FCSTD DOCUMENT  (FreeCAD 0.18.1R)
Label: Clock_idea_outline
License: All rights reserved
LicenseURL: http://en.wikipedia.org/wiki/All_rights_reserved
objects: Sketcher::SketchObject×1, PartDesign::Body×1
note: 2 computed .brp shape members not serialized (recipe doc carries the construction recipe); baked Part::Feature solids carry a one-line shape summary decoded from their .brp

FEATURE [Sketcher::SketchObject] Sketch
  MapMode = 5
  Support = -> [XY_Plane]
  sketch-geometry (292):
    g0: LineSegment StartX=0 StartY=0 StartZ=0 EndX=100 EndY=0 EndZ=0
    g1: LineSegment StartX=100 StartY=0 StartZ=0 EndX=100 EndY=50 EndZ=0
    g2: LineSegment StartX=100 StartY=50 StartZ=0 EndX=0 EndY=50 EndZ=0
    g3: LineSegment StartX=0 StartY=50 StartZ=0 EndX=0 EndY=0 EndZ=0
    g4: LineSegment StartX=1.68333 StartY=3 StartZ=0 EndX=4.98333 EndY=3 EndZ=0
    g5: LineSegment StartX=4.98333 StartY=3 StartZ=0 EndX=4.98333 EndY=5.1 EndZ=0
    g6: LineSegment StartX=4.98333 StartY=5.1 StartZ=0 EndX=1.68333 EndY=5.1 EndZ=0
    g7: LineSegment StartX=1.68333 StartY=5.1 StartZ=0 EndX=1.68333 EndY=3 EndZ=0
    g8: LineSegment StartX=8.35 StartY=3 StartZ=0 EndX=11.65 EndY=3 EndZ=0
    g9: LineSegment StartX=11.65 StartY=3 StartZ=0 EndX=11.65 EndY=5.1 EndZ=0
    g10: LineSegment StartX=11.65 StartY=5.1 StartZ=0 EndX=8.35 EndY=5.1 EndZ=0
    g11: LineSegment StartX=8.35 StartY=5.1 StartZ=0 EndX=8.35 EndY=3 EndZ=0
    g12: LineSegment StartX=15.0167 StartY=3 StartZ=0 EndX=18.3167 EndY=3 EndZ=0
    g13: LineSegment StartX=18.3167 StartY=3 StartZ=0 EndX=18.3167 EndY=5.1 EndZ=0
    g14: LineSegment StartX=18.3167 StartY=5.1 StartZ=0 EndX=15.0167 EndY=5.1 EndZ=0
    g15: LineSegment StartX=15.0167 StartY=5.1 StartZ=0 EndX=15.0167 EndY=3 EndZ=0
    g16: LineSegment StartX=21.6833 StartY=3 StartZ=0 EndX=24.9833 EndY=3 EndZ=0
    g17: LineSegment StartX=24.9833 StartY=3 StartZ=0 EndX=24.9833 EndY=5.1 EndZ=0
    g18: LineSegment StartX=24.9833 StartY=5.1 StartZ=0 EndX=21.6833 EndY=5.1 EndZ=0
    g19: LineSegment StartX=21.6833 StartY=5.1 StartZ=0 EndX=21.6833 EndY=3 EndZ=0
    g20: LineSegment StartX=28.35 StartY=3 StartZ=0 EndX=31.65 EndY=3 EndZ=0
    g21: LineSegment StartX=31.65 StartY=3 StartZ=0 EndX=31.65 EndY=5.1 EndZ=0
    g22: LineSegment StartX=31.65 StartY=5.1 StartZ=0 EndX=28.35 EndY=5.1 EndZ=0
    g23: LineSegment StartX=28.35 StartY=5.1 StartZ=0 EndX=28.35 EndY=3 EndZ=0
    g24: LineSegment StartX=35.0167 StartY=3 StartZ=0 EndX=38.3167 EndY=3 EndZ=0
    g25: LineSegment StartX=38.3167 StartY=3 StartZ=0 EndX=38.3167 EndY=5.1 EndZ=0
    g26: LineSegment StartX=38.3167 StartY=5.1 StartZ=0 EndX=35.0167 EndY=5.1 EndZ=0
    g27: LineSegment StartX=35.0167 StartY=5.1 StartZ=0 EndX=35.0167 EndY=3 EndZ=0
    g28: LineSegment StartX=41.6833 StartY=3 StartZ=0 EndX=44.9833 EndY=3 EndZ=0
    g29: LineSegment StartX=44.9833 StartY=3 StartZ=0 EndX=44.9833 EndY=5.1 EndZ=0
    g30: LineSegment StartX=44.9833 StartY=5.1 StartZ=0 EndX=41.6833 EndY=5.1 EndZ=0
    g31: LineSegment StartX=41.6833 StartY=5.1 StartZ=0 EndX=41.6833 EndY=3 EndZ=0
    g32: LineSegment StartX=48.35 StartY=3 StartZ=0 EndX=51.65 EndY=3 EndZ=0
    g33: LineSegment StartX=51.65 StartY=3 StartZ=0 EndX=51.65 EndY=5.1 EndZ=0
    g34: LineSegment StartX=51.65 StartY=5.1 StartZ=0 EndX=48.35 EndY=5.1 EndZ=0
    g35: LineSegment StartX=48.35 StartY=5.1 StartZ=0 EndX=48.35 EndY=3 EndZ=0
    g36: LineSegment StartX=55.0167 StartY=3 StartZ=0 EndX=58.3167 EndY=3 EndZ=0
    g37: LineSegment StartX=58.3167 StartY=3 StartZ=0 EndX=58.3167 EndY=5.1 EndZ=0
    g38: LineSegment StartX=58.3167 StartY=5.1 StartZ=0 EndX=55.0167 EndY=5.1 EndZ=0
    g39: LineSegment StartX=55.0167 StartY=5.1 StartZ=0 EndX=55.0167 EndY=3 EndZ=0
    g40: LineSegment StartX=61.6833 StartY=3 StartZ=0 EndX=64.9833 EndY=3 EndZ=0
    g41: LineSegment StartX=64.9833 StartY=3 StartZ=0 EndX=64.9833 EndY=5.1 EndZ=0
    g42: LineSegment StartX=64.9833 StartY=5.1 StartZ=0 EndX=61.6833 EndY=5.1 EndZ=0
    g43: LineSegment StartX=61.6833 StartY=5.1 StartZ=0 EndX=61.6833 EndY=3 EndZ=0
    g44: LineSegment StartX=68.35 StartY=3 StartZ=0 EndX=71.65 EndY=3 EndZ=0
    g45: LineSegment StartX=71.65 StartY=3 StartZ=0 EndX=71.65 EndY=5.1 EndZ=0
    g46: LineSegment StartX=71.65 StartY=5.1 StartZ=0 EndX=68.35 EndY=5.1 EndZ=0
    g47: LineSegment StartX=68.35 StartY=5.1 StartZ=0 EndX=68.35 EndY=3 EndZ=0
    g48: LineSegment StartX=75.0167 StartY=3 StartZ=0 EndX=78.3167 EndY=3 EndZ=0
    g49: LineSegment StartX=78.3167 StartY=3 StartZ=0 EndX=78.3167 EndY=5.1 EndZ=0
    g50: LineSegment StartX=78.3167 StartY=5.1 StartZ=0 EndX=75.0167 EndY=5.1 EndZ=0
    g51: LineSegment StartX=75.0167 StartY=5.1 StartZ=0 EndX=75.0167 EndY=3 EndZ=0
    g52: LineSegment StartX=81.6833 StartY=3 StartZ=0 EndX=84.9833 EndY=3 EndZ=0
    g53: LineSegment StartX=84.9833 StartY=3 StartZ=0 EndX=84.9833 EndY=5.1 EndZ=0
    g54: LineSegment StartX=84.9833 StartY=5.1 StartZ=0 EndX=81.6833 EndY=5.1 EndZ=0
    g55: LineSegment StartX=81.6833 StartY=5.1 StartZ=0 EndX=81.6833 EndY=3 EndZ=0
    g56: LineSegment StartX=88.35 StartY=3 StartZ=0 EndX=91.65 EndY=3 EndZ=0
    g57: LineSegment StartX=91.65 StartY=3 StartZ=0 EndX=91.65 EndY=5.1 EndZ=0
    g58: LineSegment StartX=91.65 StartY=5.1 StartZ=0 EndX=88.35 EndY=5.1 EndZ=0
    g59: LineSegment StartX=88.35 StartY=5.1 StartZ=0 EndX=88.35 EndY=3 EndZ=0
    g60: LineSegment StartX=95.0167 StartY=3 StartZ=0 EndX=98.3167 EndY=3 EndZ=0
    g61: LineSegment StartX=98.3167 StartY=3 StartZ=0 EndX=98.3167 EndY=5.1 EndZ=0
    g62: LineSegment StartX=98.3167 StartY=5.1 StartZ=0 EndX=95.0167 EndY=5.1 EndZ=0
    g63: LineSegment StartX=95.0167 StartY=5.1 StartZ=0 EndX=95.0167 EndY=3 EndZ=0
    g64: LineSegment StartX=1.68333 StartY=8.1 StartZ=0 EndX=4.98333 EndY=8.1 EndZ=0
    g65: LineSegment StartX=4.98333 StartY=8.1 StartZ=0 EndX=4.98333 EndY=10.2 EndZ=0
    g66: LineSegment StartX=4.98333 StartY=10.2 StartZ=0 EndX=1.68333 EndY=10.2 EndZ=0
    g67: LineSegment StartX=1.68333 StartY=10.2 StartZ=0 EndX=1.68333 EndY=8.1 EndZ=0
    g68: LineSegment StartX=8.35 StartY=8.1 StartZ=0 EndX=11.65 EndY=8.1 EndZ=0
    g69: LineSegment StartX=11.65 StartY=8.1 StartZ=0 EndX=11.65 EndY=10.2 EndZ=0
    g70: LineSegment StartX=11.65 StartY=10.2 StartZ=0 EndX=8.35 EndY=10.2 EndZ=0
    g71: LineSegment StartX=8.35 StartY=10.2 StartZ=0 EndX=8.35 EndY=8.1 EndZ=0
    g72: LineSegment StartX=15.0167 StartY=8.1 StartZ=0 EndX=18.3167 EndY=8.1 EndZ=0
    g73: LineSegment StartX=18.3167 StartY=8.1 StartZ=0 EndX=18.3167 EndY=10.2 EndZ=0
    g74: LineSegment StartX=18.3167 StartY=10.2 StartZ=0 EndX=15.0167 EndY=10.2 EndZ=0
    g75: LineSegment StartX=15.0167 StartY=10.2 StartZ=0 EndX=15.0167 EndY=8.1 EndZ=0
    g76: LineSegment StartX=21.6833 StartY=8.1 StartZ=0 EndX=24.9833 EndY=8.1 EndZ=0
    g77: LineSegment StartX=24.9833 StartY=8.1 StartZ=0 EndX=24.9833 EndY=10.2 EndZ=0
    g78: LineSegment StartX=24.9833 StartY=10.2 StartZ=0 EndX=21.6833 EndY=10.2 EndZ=0
    g79: LineSegment StartX=21.6833 StartY=10.2 StartZ=0 EndX=21.6833 EndY=8.1 EndZ=0
    g80: LineSegment StartX=28.35 StartY=8.1 StartZ=0 EndX=31.65 EndY=8.1 EndZ=0
    g81: LineSegment StartX=31.65 StartY=8.1 StartZ=0 EndX=31.65 EndY=10.2 EndZ=0
    g82: LineSegment StartX=31.65 StartY=10.2 StartZ=0 EndX=28.35 EndY=10.2 EndZ=0
    g83: LineSegment StartX=28.35 StartY=10.2 StartZ=0 EndX=28.35 EndY=8.1 EndZ=0
    g84: LineSegment StartX=35.0167 StartY=8.1 StartZ=0 EndX=38.3167 EndY=8.1 EndZ=0
    g85: LineSegment StartX=38.3167 StartY=8.1 StartZ=0 EndX=38.3167 EndY=10.2 EndZ=0
    g86: LineSegment StartX=38.3167 StartY=10.2 StartZ=0 EndX=35.0167 EndY=10.2 EndZ=0
    g87: LineSegment StartX=35.0167 StartY=10.2 StartZ=0 EndX=35.0167 EndY=8.1 EndZ=0
    g88: LineSegment StartX=41.6833 StartY=8.1 StartZ=0 EndX=44.9833 EndY=8.1 EndZ=0
    g89: LineSegment StartX=44.9833 StartY=8.1 StartZ=0 EndX=44.9833 EndY=10.2 EndZ=0
    g90: LineSegment StartX=44.9833 StartY=10.2 StartZ=0 EndX=41.6833 EndY=10.2 EndZ=0
    g91: LineSegment StartX=41.6833 StartY=10.2 StartZ=0 EndX=41.6833 EndY=8.1 EndZ=0
    g92: LineSegment StartX=48.35 StartY=8.1 StartZ=0 EndX=51.65 EndY=8.1 EndZ=0
    g93: LineSegment StartX=51.65 StartY=8.1 StartZ=0 EndX=51.65 EndY=10.2 EndZ=0
    g94: LineSegment StartX=51.65 StartY=10.2 StartZ=0 EndX=48.35 EndY=10.2 EndZ=0
    g95: LineSegment StartX=48.35 StartY=10.2 StartZ=0 EndX=48.35 EndY=8.1 EndZ=0
    g96: LineSegment StartX=55.0167 StartY=8.1 StartZ=0 EndX=58.3167 EndY=8.1 EndZ=0
    g97: LineSegment StartX=58.3167 StartY=8.1 StartZ=0 EndX=58.3167 EndY=10.2 EndZ=0
    g98: LineSegment StartX=58.3167 StartY=10.2 StartZ=0 EndX=55.0167 EndY=10.2 EndZ=0
    g99: LineSegment StartX=55.0167 StartY=10.2 StartZ=0 EndX=55.0167 EndY=8.1 EndZ=0
    g100: LineSegment StartX=61.6833 StartY=8.1 StartZ=0 EndX=64.9833 EndY=8.1 EndZ=0
    g101: LineSegment StartX=64.9833 StartY=8.1 StartZ=0 EndX=64.9833 EndY=10.2 EndZ=0
    g102: LineSegment StartX=64.9833 StartY=10.2 StartZ=0 EndX=61.6833 EndY=10.2 EndZ=0
    g103: LineSegment StartX=61.6833 StartY=10.2 StartZ=0 EndX=61.6833 EndY=8.1 EndZ=0
    g104: LineSegment StartX=68.35 StartY=8.1 StartZ=0 EndX=71.65 EndY=8.1 EndZ=0
    g105: LineSegment StartX=71.65 StartY=8.1 StartZ=0 EndX=71.65 EndY=10.2 EndZ=0
    g106: LineSegment StartX=71.65 StartY=10.2 StartZ=0 EndX=68.35 EndY=10.2 EndZ=0
    g107: LineSegment StartX=68.35 StartY=10.2 StartZ=0 EndX=68.35 EndY=8.1 EndZ=0
    g108: LineSegment StartX=75.0167 StartY=8.1 StartZ=0 EndX=78.3167 EndY=8.1 EndZ=0
    g109: LineSegment StartX=78.3167 StartY=8.1 StartZ=0 EndX=78.3167 EndY=10.2 EndZ=0
    g110: LineSegment StartX=78.3167 StartY=10.2 StartZ=0 EndX=75.0167 EndY=10.2 EndZ=0
    g111: LineSegment StartX=75.0167 StartY=10.2 StartZ=0 EndX=75.0167 EndY=8.1 EndZ=0
    g112: LineSegment StartX=81.6833 StartY=8.1 StartZ=0 EndX=84.9833 EndY=8.1 EndZ=0
    g113: LineSegment StartX=84.9833 StartY=8.1 StartZ=0 EndX=84.9833 EndY=10.2 EndZ=0
    g114: LineSegment StartX=84.9833 StartY=10.2 StartZ=0 EndX=81.6833 EndY=10.2 EndZ=0
    g115: LineSegment StartX=81.6833 StartY=10.2 StartZ=0 EndX=81.6833 EndY=8.1 EndZ=0
    g116: LineSegment StartX=88.35 StartY=8.1 StartZ=0 EndX=91.65 EndY=8.1 EndZ=0
    g117: LineSegment StartX=91.65 StartY=8.1 StartZ=0 EndX=91.65 EndY=10.2 EndZ=0
    g118: LineSegment StartX=91.65 StartY=10.2 StartZ=0 EndX=88.35 EndY=10.2 EndZ=0
    g119: LineSegment StartX=88.35 StartY=10.2 StartZ=0 EndX=88.35 EndY=8.1 EndZ=0
    g120: LineSegment StartX=95.0167 StartY=8.1 StartZ=0 EndX=98.3167 EndY=8.1 EndZ=0
    g121: LineSegment StartX=98.3167 StartY=8.1 StartZ=0 EndX=98.3167 EndY=10.2 EndZ=0
    g122: LineSegment StartX=98.3167 StartY=10.2 StartZ=0 EndX=95.0167 EndY=10.2 EndZ=0
    g123: LineSegment StartX=95.0167 StartY=10.2 StartZ=0 EndX=95.0167 EndY=8.1 EndZ=0
    g124: LineSegment StartX=1.68333 StartY=13.2 StartZ=0 EndX=4.98333 EndY=13.2 EndZ=0
    g125: LineSegment StartX=4.98333 StartY=13.2 StartZ=0 EndX=4.98333 EndY=15.3 EndZ=0
    g126: LineSegment StartX=4.98333 StartY=15.3 StartZ=0 EndX=1.68333 EndY=15.3 EndZ=0
    g127: LineSegment StartX=1.68333 StartY=15.3 StartZ=0 EndX=1.68333 EndY=13.2 EndZ=0
    g128: LineSegment StartX=8.35 StartY=13.2 StartZ=0 EndX=11.65 EndY=13.2 EndZ=0
    g129: LineSegment StartX=11.65 StartY=13.2 StartZ=0 EndX=11.65 EndY=15.3 EndZ=0
    g130: LineSegment StartX=11.65 StartY=15.3 StartZ=0 EndX=8.35 EndY=15.3 EndZ=0
    g131: LineSegment StartX=8.35 StartY=15.3 StartZ=0 EndX=8.35 EndY=13.2 EndZ=0
    g132: LineSegment StartX=15.0167 StartY=13.2 StartZ=0 EndX=18.3167 EndY=13.2 EndZ=0
    g133: LineSegment StartX=18.3167 StartY=13.2 StartZ=0 EndX=18.3167 EndY=15.3 EndZ=0
    g134: LineSegment StartX=18.3167 StartY=15.3 StartZ=0 EndX=15.0167 EndY=15.3 EndZ=0
    g135: LineSegment StartX=15.0167 StartY=15.3 StartZ=0 EndX=15.0167 EndY=13.2 EndZ=0
    g136: LineSegment StartX=21.6833 StartY=13.2 StartZ=0 EndX=24.9833 EndY=13.2 EndZ=0
    g137: LineSegment StartX=24.9833 StartY=13.2 StartZ=0 EndX=24.9833 EndY=15.3 EndZ=0
    g138: LineSegment StartX=24.9833 StartY=15.3 StartZ=0 EndX=21.6833 EndY=15.3 EndZ=0
    g139: LineSegment StartX=21.6833 StartY=15.3 StartZ=0 EndX=21.6833 EndY=13.2 EndZ=0
    g140: LineSegment StartX=28.35 StartY=13.2 StartZ=0 EndX=31.65 EndY=13.2 EndZ=0
    g141: LineSegment StartX=31.65 StartY=13.2 StartZ=0 EndX=31.65 EndY=15.3 EndZ=0
    g142: LineSegment StartX=31.65 StartY=15.3 StartZ=0 EndX=28.35 EndY=15.3 EndZ=0
    g143: LineSegment StartX=28.35 StartY=15.3 StartZ=0 EndX=28.35 EndY=13.2 EndZ=0
    g144: LineSegment StartX=35.0167 StartY=13.2 StartZ=0 EndX=38.3167 EndY=13.2 EndZ=0
    g145: LineSegment StartX=38.3167 StartY=13.2 StartZ=0 EndX=38.3167 EndY=15.3 EndZ=0
    g146: LineSegment StartX=38.3167 StartY=15.3 StartZ=0 EndX=35.0167 EndY=15.3 EndZ=0
    g147: LineSegment StartX=35.0167 StartY=15.3 StartZ=0 EndX=35.0167 EndY=13.2 EndZ=0
    g148: LineSegment StartX=41.6833 StartY=13.2 StartZ=0 EndX=44.9833 EndY=13.2 EndZ=0
    g149: LineSegment StartX=44.9833 StartY=13.2 StartZ=0 EndX=44.9833 EndY=15.3 EndZ=0
    g150: LineSegment StartX=44.9833 StartY=15.3 StartZ=0 EndX=41.6833 EndY=15.3 EndZ=0
    g151: LineSegment StartX=41.6833 StartY=15.3 StartZ=0 EndX=41.6833 EndY=13.2 EndZ=0
    g152: LineSegment StartX=48.35 StartY=13.2 StartZ=0 EndX=51.65 EndY=13.2 EndZ=0
    g153: LineSegment StartX=51.65 StartY=13.2 StartZ=0 EndX=51.65 EndY=15.3 EndZ=0
    g154: LineSegment StartX=51.65 StartY=15.3 StartZ=0 EndX=48.35 EndY=15.3 EndZ=0
    g155: LineSegment StartX=48.35 StartY=15.3 StartZ=0 EndX=48.35 EndY=13.2 EndZ=0
    g156: LineSegment StartX=55.0167 StartY=13.2 StartZ=0 EndX=58.3167 EndY=13.2 EndZ=0
    g157: LineSegment StartX=58.3167 StartY=13.2 StartZ=0 EndX=58.3167 EndY=15.3 EndZ=0
    g158: LineSegment StartX=58.3167 StartY=15.3 StartZ=0 EndX=55.0167 EndY=15.3 EndZ=0
    g159: LineSegment StartX=55.0167 StartY=15.3 StartZ=0 EndX=55.0167 EndY=13.2 EndZ=0
    g160: LineSegment StartX=61.6833 StartY=13.2 StartZ=0 EndX=64.9833 EndY=13.2 EndZ=0
    g161: LineSegment StartX=64.9833 StartY=13.2 StartZ=0 EndX=64.9833 EndY=15.3 EndZ=0
    g162: LineSegment StartX=64.9833 StartY=15.3 StartZ=0 EndX=61.6833 EndY=15.3 EndZ=0
    g163: LineSegment StartX=61.6833 StartY=15.3 StartZ=0 EndX=61.6833 EndY=13.2 EndZ=0
    g164: LineSegment StartX=68.35 StartY=13.2 StartZ=0 EndX=71.65 EndY=13.2 EndZ=0
    g165: LineSegment StartX=71.65 StartY=13.2 StartZ=0 EndX=71.65 EndY=15.3 EndZ=0
    g166: LineSegment StartX=71.65 StartY=15.3 StartZ=0 EndX=68.35 EndY=15.3 EndZ=0
    g167: LineSegment StartX=68.35 StartY=15.3 StartZ=0 EndX=68.35 EndY=13.2 EndZ=0
    g168: LineSegment StartX=75.0167 StartY=13.2 StartZ=0 EndX=78.3167 EndY=13.2 EndZ=0
    g169: LineSegment StartX=78.3167 StartY=13.2 StartZ=0 EndX=78.3167 EndY=15.3 EndZ=0
    g170: LineSegment StartX=78.3167 StartY=15.3 StartZ=0 EndX=75.0167 EndY=15.3 EndZ=0
    g171: LineSegment StartX=75.0167 StartY=15.3 StartZ=0 EndX=75.0167 EndY=13.2 EndZ=0
    g172: LineSegment StartX=81.6833 StartY=13.2 StartZ=0 EndX=84.9833 EndY=13.2 EndZ=0
    g173: LineSegment StartX=84.9833 StartY=13.2 StartZ=0 EndX=84.9833 EndY=15.3 EndZ=0
    g174: LineSegment StartX=84.9833 StartY=15.3 StartZ=0 EndX=81.6833 EndY=15.3 EndZ=0
    g175: LineSegment StartX=81.6833 StartY=15.3 StartZ=0 EndX=81.6833 EndY=13.2 EndZ=0
    g176: LineSegment StartX=88.35 StartY=13.2 StartZ=0 EndX=91.65 EndY=13.2 EndZ=0
    g177: LineSegment StartX=91.65 StartY=13.2 StartZ=0 EndX=91.65 EndY=15.3 EndZ=0
    g178: LineSegment StartX=91.65 StartY=15.3 StartZ=0 EndX=88.35 EndY=15.3 EndZ=0
    g179: LineSegment StartX=88.35 StartY=15.3 StartZ=0 EndX=88.35 EndY=13.2 EndZ=0
    g180: LineSegment StartX=95.0167 StartY=13.2 StartZ=0 EndX=98.3167 EndY=13.2 EndZ=0
    g181: LineSegment StartX=98.3167 StartY=13.2 StartZ=0 EndX=98.3167 EndY=15.3 EndZ=0
    g182: LineSegment StartX=98.3167 StartY=15.3 StartZ=0 EndX=95.0167 EndY=15.3 EndZ=0
    g183: LineSegment StartX=95.0167 StartY=15.3 StartZ=0 EndX=95.0167 EndY=13.2 EndZ=0
    g184: LineSegment StartX=2.51667 StartY=25.5 StartZ=0 EndX=5.81667 EndY=25.5 EndZ=0
    g185: LineSegment StartX=5.81667 StartY=25.5 StartZ=0 EndX=5.81667 EndY=27.6 EndZ=0
    g186: LineSegment StartX=5.81667 StartY=27.6 StartZ=0 EndX=2.51667 EndY=27.6 EndZ=0
    g187: LineSegment StartX=2.51667 StartY=27.6 StartZ=0 EndX=2.51667 EndY=25.5 EndZ=0
    g188: LineSegment StartX=10.85 StartY=25.5 StartZ=0 EndX=14.15 EndY=25.5 EndZ=0
    g189: LineSegment StartX=14.15 StartY=25.5 StartZ=0 EndX=14.15 EndY=27.6 EndZ=0
    g190: LineSegment StartX=14.15 StartY=27.6 StartZ=0 EndX=10.85 EndY=27.6 EndZ=0
    g191: LineSegment StartX=10.85 StartY=27.6 StartZ=0 EndX=10.85 EndY=25.5 EndZ=0
    g192: LineSegment StartX=19.1833 StartY=25.5 StartZ=0 EndX=22.4833 EndY=25.5 EndZ=0
    g193: LineSegment StartX=22.4833 StartY=25.5 StartZ=0 EndX=22.4833 EndY=27.6 EndZ=0
    g194: LineSegment StartX=22.4833 StartY=27.6 StartZ=0 EndX=19.1833 EndY=27.6 EndZ=0
    g195: LineSegment StartX=19.1833 StartY=27.6 StartZ=0 EndX=19.1833 EndY=25.5 EndZ=0
    g196: LineSegment StartX=27.5167 StartY=25.5 StartZ=0 EndX=30.8167 EndY=25.5 EndZ=0
    g197: LineSegment StartX=30.8167 StartY=25.5 StartZ=0 EndX=30.8167 EndY=27.6 EndZ=0
    g198: LineSegment StartX=30.8167 StartY=27.6 StartZ=0 EndX=27.5167 EndY=27.6 EndZ=0
    g199: LineSegment StartX=27.5167 StartY=27.6 StartZ=0 EndX=27.5167 EndY=25.5 EndZ=0
    g200: LineSegment StartX=35.85 StartY=25.5 StartZ=0 EndX=39.15 EndY=25.5 EndZ=0
    g201: LineSegment StartX=39.15 StartY=25.5 StartZ=0 EndX=39.15 EndY=27.6 EndZ=0
    g202: LineSegment StartX=39.15 StartY=27.6 StartZ=0 EndX=35.85 EndY=27.6 EndZ=0
    g203: LineSegment StartX=35.85 StartY=27.6 StartZ=0 EndX=35.85 EndY=25.5 EndZ=0
    g204: LineSegment StartX=44.1833 StartY=25.5 StartZ=0 EndX=47.4833 EndY=25.5 EndZ=0
    g205: LineSegment StartX=47.4833 StartY=25.5 StartZ=0 EndX=47.4833 EndY=27.6 EndZ=0
    g206: LineSegment StartX=47.4833 StartY=27.6 StartZ=0 EndX=44.1833 EndY=27.6 EndZ=0
    g207: LineSegment StartX=44.1833 StartY=27.6 StartZ=0 EndX=44.1833 EndY=25.5 EndZ=0
    g208: LineSegment StartX=52.5167 StartY=25.5 StartZ=0 EndX=55.8167 EndY=25.5 EndZ=0
    g209: LineSegment StartX=55.8167 StartY=25.5 StartZ=0 EndX=55.8167 EndY=27.6 EndZ=0
    g210: LineSegment StartX=55.8167 StartY=27.6 StartZ=0 EndX=52.5167 EndY=27.6 EndZ=0
    g211: LineSegment StartX=52.5167 StartY=27.6 StartZ=0 EndX=52.5167 EndY=25.5 EndZ=0
    g212: LineSegment StartX=60.85 StartY=25.5 StartZ=0 EndX=64.15 EndY=25.5 EndZ=0
    g213: LineSegment StartX=64.15 StartY=25.5 StartZ=0 EndX=64.15 EndY=27.6 EndZ=0
    g214: LineSegment StartX=64.15 StartY=27.6 StartZ=0 EndX=60.85 EndY=27.6 EndZ=0
    g215: LineSegment StartX=60.85 StartY=27.6 StartZ=0 EndX=60.85 EndY=25.5 EndZ=0
    g216: LineSegment StartX=69.1833 StartY=25.5 StartZ=0 EndX=72.4833 EndY=25.5 EndZ=0
    g217: LineSegment StartX=72.4833 StartY=25.5 StartZ=0 EndX=72.4833 EndY=27.6 EndZ=0
    g218: LineSegment StartX=72.4833 StartY=27.6 StartZ=0 EndX=69.1833 EndY=27.6 EndZ=0
    g219: LineSegment StartX=69.1833 StartY=27.6 StartZ=0 EndX=69.1833 EndY=25.5 EndZ=0
    g220: LineSegment StartX=77.5167 StartY=25.5 StartZ=0 EndX=80.8167 EndY=25.5 EndZ=0
    g221: LineSegment StartX=80.8167 StartY=25.5 StartZ=0 EndX=80.8167 EndY=27.6 EndZ=0
    g222: LineSegment StartX=80.8167 StartY=27.6 StartZ=0 EndX=77.5167 EndY=27.6 EndZ=0
    g223: LineSegment StartX=77.5167 StartY=27.6 StartZ=0 EndX=77.5167 EndY=25.5 EndZ=0
    g224: LineSegment StartX=85.85 StartY=25.5 StartZ=0 EndX=89.15 EndY=25.5 EndZ=0
    g225: LineSegment StartX=89.15 StartY=25.5 StartZ=0 EndX=89.15 EndY=27.6 EndZ=0
    g226: LineSegment StartX=89.15 StartY=27.6 StartZ=0 EndX=85.85 EndY=27.6 EndZ=0
    g227: LineSegment StartX=85.85 StartY=27.6 StartZ=0 EndX=85.85 EndY=25.5 EndZ=0
    g228: LineSegment StartX=94.1833 StartY=25.5 StartZ=0 EndX=97.4833 EndY=25.5 EndZ=0
    g229: LineSegment StartX=97.4833 StartY=25.5 StartZ=0 EndX=97.4833 EndY=27.6 EndZ=0
    g230: LineSegment StartX=97.4833 StartY=27.6 StartZ=0 EndX=94.1833 EndY=27.6 EndZ=0
    g231: LineSegment StartX=94.1833 StartY=27.6 StartZ=0 EndX=94.1833 EndY=25.5 EndZ=0
    g232: LineSegment StartX=1.68333 StartY=18.3 StartZ=0 EndX=4.98333 EndY=18.3 EndZ=0
    g233: LineSegment StartX=4.98333 StartY=18.3 StartZ=0 EndX=4.98333 EndY=20.4 EndZ=0
    g234: LineSegment StartX=4.98333 StartY=20.4 StartZ=0 EndX=1.68333 EndY=20.4 EndZ=0
    g235: LineSegment StartX=1.68333 StartY=20.4 StartZ=0 EndX=1.68333 EndY=18.3 EndZ=0
    g236: LineSegment StartX=8.35 StartY=18.3 StartZ=0 EndX=11.65 EndY=18.3 EndZ=0
    g237: LineSegment StartX=11.65 StartY=18.3 StartZ=0 EndX=11.65 EndY=20.4 EndZ=0
    g238: LineSegment StartX=11.65 StartY=20.4 StartZ=0 EndX=8.35 EndY=20.4 EndZ=0
    g239: LineSegment StartX=8.35 StartY=20.4 StartZ=0 EndX=8.35 EndY=18.3 EndZ=0
    g240: LineSegment StartX=15.0167 StartY=18.3 StartZ=0 EndX=18.3167 EndY=18.3 EndZ=0
    g241: LineSegment StartX=18.3167 StartY=18.3 StartZ=0 EndX=18.3167 EndY=20.4 EndZ=0
    g242: LineSegment StartX=18.3167 StartY=20.4 StartZ=0 EndX=15.0167 EndY=20.4 EndZ=0
    g243: LineSegment StartX=15.0167 StartY=20.4 StartZ=0 EndX=15.0167 EndY=18.3 EndZ=0
    g244: LineSegment StartX=21.6833 StartY=18.3 StartZ=0 EndX=24.9833 EndY=18.3 EndZ=0
    g245: LineSegment StartX=24.9833 StartY=18.3 StartZ=0 EndX=24.9833 EndY=20.4 EndZ=0
    g246: LineSegment StartX=24.9833 StartY=20.4 StartZ=0 EndX=21.6833 EndY=20.4 EndZ=0
    g247: LineSegment StartX=21.6833 StartY=20.4 StartZ=0 EndX=21.6833 EndY=18.3 EndZ=0
    g248: LineSegment StartX=28.35 StartY=18.3 StartZ=0 EndX=31.65 EndY=18.3 EndZ=0
    g249: LineSegment StartX=31.65 StartY=18.3 StartZ=0 EndX=31.65 EndY=20.4 EndZ=0
    g250: LineSegment StartX=31.65 StartY=20.4 StartZ=0 EndX=28.35 EndY=20.4 EndZ=0
    g251: LineSegment StartX=28.35 StartY=20.4 StartZ=0 EndX=28.35 EndY=18.3 EndZ=0
    g252: LineSegment StartX=35.0167 StartY=18.3 StartZ=0 EndX=38.3167 EndY=18.3 EndZ=0
    g253: LineSegment StartX=38.3167 StartY=18.3 StartZ=0 EndX=38.3167 EndY=20.4 EndZ=0
    g254: LineSegment StartX=38.3167 StartY=20.4 StartZ=0 EndX=35.0167 EndY=20.4 EndZ=0
    g255: LineSegment StartX=35.0167 StartY=20.4 StartZ=0 EndX=35.0167 EndY=18.3 EndZ=0
    g256: LineSegment StartX=41.6833 StartY=18.3 StartZ=0 EndX=44.9833 EndY=18.3 EndZ=0
    g257: LineSegment StartX=44.9833 StartY=18.3 StartZ=0 EndX=44.9833 EndY=20.4 EndZ=0
    g258: LineSegment StartX=44.9833 StartY=20.4 StartZ=0 EndX=41.6833 EndY=20.4 EndZ=0
    g259: LineSegment StartX=41.6833 StartY=20.4 StartZ=0 EndX=41.6833 EndY=18.3 EndZ=0
    g260: LineSegment StartX=48.35 StartY=18.3 StartZ=0 EndX=51.65 EndY=18.3 EndZ=0
    g261: LineSegment StartX=51.65 StartY=18.3 StartZ=0 EndX=51.65 EndY=20.4 EndZ=0
    g262: LineSegment StartX=51.65 StartY=20.4 StartZ=0 EndX=48.35 EndY=20.4 EndZ=0
    g263: LineSegment StartX=48.35 StartY=20.4 StartZ=0 EndX=48.35 EndY=18.3 EndZ=0
    g264: LineSegment StartX=55.0167 StartY=18.3 StartZ=0 EndX=58.3167 EndY=18.3 EndZ=0
    g265: LineSegment StartX=58.3167 StartY=18.3 StartZ=0 EndX=58.3167 EndY=20.4 EndZ=0
    g266: LineSegment StartX=58.3167 StartY=20.4 StartZ=0 EndX=55.0167 EndY=20.4 EndZ=0
    g267: LineSegment StartX=55.0167 StartY=20.4 StartZ=0 EndX=55.0167 EndY=18.3 EndZ=0
    g268: LineSegment StartX=61.6833 StartY=18.3 StartZ=0 EndX=64.9833 EndY=18.3 EndZ=0
    g269: LineSegment StartX=64.9833 StartY=18.3 StartZ=0 EndX=64.9833 EndY=20.4 EndZ=0
    g270: LineSegment StartX=64.9833 StartY=20.4 StartZ=0 EndX=61.6833 EndY=20.4 EndZ=0
    g271: LineSegment StartX=61.6833 StartY=20.4 StartZ=0 EndX=61.6833 EndY=18.3 EndZ=0
    g272: LineSegment StartX=68.35 StartY=18.3 StartZ=0 EndX=71.65 EndY=18.3 EndZ=0
    g273: LineSegment StartX=71.65 StartY=18.3 StartZ=0 EndX=71.65 EndY=20.4 EndZ=0
    g274: LineSegment StartX=71.65 StartY=20.4 StartZ=0 EndX=68.35 EndY=20.4 EndZ=0
    g275: LineSegment StartX=68.35 StartY=20.4 StartZ=0 EndX=68.35 EndY=18.3 EndZ=0
    g276: LineSegment StartX=75.0167 StartY=18.3 StartZ=0 EndX=78.3167 EndY=18.3 EndZ=0
    g277: LineSegment StartX=78.3167 StartY=18.3 StartZ=0 EndX=78.3167 EndY=20.4 EndZ=0
    g278: LineSegment StartX=78.3167 StartY=20.4 StartZ=0 EndX=75.0167 EndY=20.4 EndZ=0
    g279: LineSegment StartX=75.0167 StartY=20.4 StartZ=0 EndX=75.0167 EndY=18.3 EndZ=0
    g280: LineSegment StartX=81.6833 StartY=18.3 StartZ=0 EndX=84.9833 EndY=18.3 EndZ=0
    g281: LineSegment StartX=84.9833 StartY=18.3 StartZ=0 EndX=84.9833 EndY=20.4 EndZ=0
    g282: LineSegment StartX=84.9833 StartY=20.4 StartZ=0 EndX=81.6833 EndY=20.4 EndZ=0
    g283: LineSegment StartX=81.6833 StartY=20.4 StartZ=0 EndX=81.6833 EndY=18.3 EndZ=0
    g284: LineSegment StartX=88.35 StartY=18.3 StartZ=0 EndX=91.65 EndY=18.3 EndZ=0
    g285: LineSegment StartX=91.65 StartY=18.3 StartZ=0 EndX=91.65 EndY=20.4 EndZ=0
    g286: LineSegment StartX=91.65 StartY=20.4 StartZ=0 EndX=88.35 EndY=20.4 EndZ=0
    g287: LineSegment StartX=88.35 StartY=20.4 StartZ=0 EndX=88.35 EndY=18.3 EndZ=0
    g288: LineSegment StartX=95.0167 StartY=18.3 StartZ=0 EndX=98.3167 EndY=18.3 EndZ=0
    g289: LineSegment StartX=98.3167 StartY=18.3 StartZ=0 EndX=98.3167 EndY=20.4 EndZ=0
    g290: LineSegment StartX=98.3167 StartY=20.4 StartZ=0 EndX=95.0167 EndY=20.4 EndZ=0
    g291: LineSegment StartX=95.0167 StartY=20.4 StartZ=0 EndX=95.0167 EndY=18.3 EndZ=0
  constraints (875):
    c: Coincident(g0,g1)
    c: Coincident(g1,g2)
    c: Coincident(g2,g3)
    c: Coincident(g3,g0)
    c: Horizontal(g0)
    c: Horizontal(g2)
    c: Vertical(g1)
    c: Vertical(g3)
    c: Coincident(g0,g-1)
    c: DistanceX(g0,g0) = 100
    c: DistanceY(g1,g1) = 50
    c: Coincident(g4,g5)
    c: Coincident(g5,g6)
    c: Coincident(g6,g7)
    c: Coincident(g7,g4)
    c: Horizontal(g4)
    c: Horizontal(g6)
    c: Vertical(g5)
    c: Vertical(g7)
    c: DistanceX(g4,g4) = 3.3
    c: DistanceY(g5,g5) = 2.1
    c: Distance(g4,g0) = 3
    c: Distance(g6,g3) = 1.68333
    c: Coincident(g8,g9)
    c: Coincident(g9,g10)
    c: Coincident(g10,g11)
    c: Coincident(g11,g8)
    c: Horizontal(g8)
    c: Horizontal(g10)
    c: Vertical(g9)
    c: Vertical(g11)
    c: Equal(g4,g8) = 3.3
    c: Equal(g5,g9) = 2.1
    c: Distance(g5,g10) = 3.36667
    c: Distance(g8,g0) = 3
    c: Coincident(g12,g13)
    c: Coincident(g13,g14)
    c: Coincident(g14,g15)
    c: Coincident(g15,g12)
    c: Horizontal(g12)
    c: Horizontal(g14)
    c: Vertical(g13)
    c: Vertical(g15)
    c: Equal(g4,g12) = 3.3
    c: Equal(g5,g13) = 2.1
    c: Coincident(g16,g17)
    c: Coincident(g17,g18)
    c: Coincident(g18,g19)
    c: Coincident(g19,g16)
    c: Horizontal(g16)
    c: Horizontal(g18)
    c: Vertical(g17)
    c: Vertical(g19)
    c: Equal(g12,g16) = 3.3
    c: Equal(g13,g17) = 2.1
    c: Distance(g13,g18) = 3.36667
    c: Distance(g9,g14) = 3.36667
    c: Distance(g16,g0) = 3
    c: Distance(g12,g0) = 3
    c: Coincident(g20,g21)
    c: Coincident(g21,g22)
    c: Coincident(g22,g23)
    c: Coincident(g23,g20)
    c: Horizontal(g20)
    c: Horizontal(g22)
    c: Vertical(g21)
    c: Vertical(g23)
    c: Equal(g4,g20) = 3.3
    c: Equal(g5,g21) = 2.1
    c: Coincident(g24,g25)
    c: Coincident(g25,g26)
    c: Coincident(g26,g27)
    c: Coincident(g27,g24)
    c: Horizontal(g24)
    c: Horizontal(g26)
    c: Vertical(g25)
    c: Vertical(g27)
    c: Equal(g20,g24) = 3.3
    c: Equal(g21,g25) = 2.1
    c: Distance(g21,g26) = 3.36667
    c: Coincident(g28,g29)
    c: Coincident(g29,g30)
    c: Coincident(g30,g31)
    c: Coincident(g31,g28)
    c: Horizontal(g28)
    c: Horizontal(g30)
    c: Vertical(g29)
    c: Vertical(g31)
    c: Equal(g20,g28) = 3.3
    c: Equal(g21,g29) = 2.1
    c: Coincident(g32,g33)
    c: Coincident(g33,g34)
    c: Coincident(g34,g35)
    c: Coincident(g35,g32)
    c: Horizontal(g32)
    c: Horizontal(g34)
    c: Vertical(g33)
    c: Vertical(g35)
    c: Equal(g28,g32) = 3.3
    c: Equal(g29,g33) = 2.1
    c: Distance(g29,g34) = 3.36667
    c: Distance(g25,g30) = 3.36667
    c: Distance(g17,g22) = 3.36667
    c: Distance(g20,g0) = 3
    c: Distance(g24,g0) = 3
    c: Distance(g28,g0) = 3
    c: Distance(g32,g0) = 3
    c: Coincident(g36,g37)
    c: Coincident(g37,g38)
    c: Coincident(g38,g39)
    c: Coincident(g39,g36)
    c: Horizontal(g36)
    c: Horizontal(g38)
    c: Vertical(g37)
    c: Vertical(g39)
    c: Equal(g4,g36) = 3.3
    c: Equal(g5,g37) = 2.1
    c: Coincident(g40,g41)
    c: Coincident(g41,g42)
    c: Coincident(g42,g43)
    c: Coincident(g43,g40)
    c: Horizontal(g40)
    c: Horizontal(g42)
    c: Vertical(g41)
    c: Vertical(g43)
    c: Equal(g36,g40) = 3.3
    c: Equal(g37,g41) = 2.1
    c: Distance(g37,g42) = 3.36667
    c: Coincident(g44,g45)
    c: Coincident(g45,g46)
    c: Coincident(g46,g47)
    c: Coincident(g47,g44)
    c: Horizontal(g44)
    c: Horizontal(g46)
    c: Vertical(g45)
    c: Vertical(g47)
    c: Equal(g36,g44) = 3.3
    c: Equal(g37,g45) = 2.1
    c: Coincident(g48,g49)
    c: Coincident(g49,g50)
    c: Coincident(g50,g51)
    c: Coincident(g51,g48)
    c: Horizontal(g48)
    c: Horizontal(g50)
    c: Vertical(g49)
    c: Vertical(g51)
    c: Equal(g44,g48) = 3.3
    c: Equal(g45,g49) = 2.1
    c: Distance(g45,g50) = 3.36667
    c: Distance(g41,g46) = 3.36667
    c: Coincident(g52,g53)
    c: Coincident(g53,g54)
    c: Coincident(g54,g55)
    c: Coincident(g55,g52)
    c: Horizontal(g52)
    c: Horizontal(g54)
    c: Vertical(g53)
    c: Vertical(g55)
    c: Equal(g36,g52) = 3.3
    c: Equal(g37,g53) = 2.1
    c: Coincident(g56,g57)
    c: Coincident(g57,g58)
    c: Coincident(g58,g59)
    c: Coincident(g59,g56)
    c: Horizontal(g56)
    c: Horizontal(g58)
    c: Vertical(g57)
    c: Vertical(g59)
    c: Equal(g52,g56) = 3.3
    c: Equal(g53,g57) = 2.1
    c: Distance(g53,g58) = 3.36667
    c: Coincident(g60,g61)
    c: Coincident(g61,g62)
    c: Coincident(g62,g63)
    c: Coincident(g63,g60)
    c: Horizontal(g60)
    c: Horizontal(g62)
    c: Vertical(g61)
    c: Vertical(g63)
    c: Equal(g52,g60) = 3.3
    c: Equal(g53,g61) = 2.1
    c: Distance(g57,g62) = 3.36667
    c: Distance(g49,g54) = 3.36667
    c: Distance(g33,g38) = 3.36667
    c: Distance(g36,g0) = 3
    c: Distance(g40,g0) = 3
    c: Distance(g44,g0) = 3
    c: Distance(g48,g0) = 3
    c: Distance(g52,g0) = 3
    c: Distance(g56,g0) = 3
    c: Distance(g60,g0) = 3
    c: Coincident(g64,g65)
    c: Coincident(g65,g66)
    c: Coincident(g66,g67)
    c: Coincident(g67,g64)
    c: Horizontal(g64)
    c: Horizontal(g66)
    c: Vertical(g65)
    c: Vertical(g67)
    c: Equal(g4,g64) = 3.3
    c: Equal(g5,g65) = 2.1
    c: Coincident(g68,g69)
    c: Coincident(g69,g70)
    c: Coincident(g70,g71)
    c: Coincident(g71,g68)
    c: Horizontal(g68)
    c: Horizontal(g70)
    c: Vertical(g69)
    c: Vertical(g71)
    c: Equal(g64,g68) = 3.3
    c: Equal(g65,g69) = 2.1
    c: Distance(g65,g70) = 3.36667
    c: Coincident(g72,g73)
    c: Coincident(g73,g74)
    c: Coincident(g74,g75)
    c: Coincident(g75,g72)
    c: Horizontal(g72)
    c: Horizontal(g74)
    c: Vertical(g73)
    c: Vertical(g75)
    c: Equal(g64,g72) = 3.3
    c: Equal(g65,g73) = 2.1
    c: Coincident(g76,g77)
    c: Coincident(g77,g78)
    c: Coincident(g78,g79)
    c: Coincident(g79,g76)
    c: Horizontal(g76)
    c: Horizontal(g78)
    c: Vertical(g77)
    c: Vertical(g79)
    c: Equal(g72,g76) = 3.3
    c: Equal(g73,g77) = 2.1
    c: Distance(g73,g78) = 3.36667
    c: Distance(g69,g74) = 3.36667
    c: Coincident(g80,g81)
    c: Coincident(g81,g82)
    c: Coincident(g82,g83)
    c: Coincident(g83,g80)
    c: Horizontal(g80)
    c: Horizontal(g82)
    c: Vertical(g81)
    c: Vertical(g83)
    c: Equal(g64,g80) = 3.3
    c: Equal(g65,g81) = 2.1
    c: Coincident(g84,g85)
    c: Coincident(g85,g86)
    c: Coincident(g86,g87)
    c: Coincident(g87,g84)
    c: Horizontal(g84)
    c: Horizontal(g86)
    c: Vertical(g85)
    c: Vertical(g87)
    c: Equal(g80,g84) = 3.3
    c: Equal(g81,g85) = 2.1
    c: Distance(g81,g86) = 3.36667
    c: Coincident(g88,g89)
    c: Coincident(g89,g90)
    c: Coincident(g90,g91)
    c: Coincident(g91,g88)
    c: Horizontal(g88)
    c: Horizontal(g90)
    c: Vertical(g89)
    c: Vertical(g91)
    c: Equal(g80,g88) = 3.3
    c: Equal(g81,g89) = 2.1
    c: Coincident(g92,g93)
    c: Coincident(g93,g94)
    c: Coincident(g94,g95)
    c: Coincident(g95,g92)
    c: Horizontal(g92)
    c: Horizontal(g94)
    c: Vertical(g93)
    c: Vertical(g95)
    c: Equal(g88,g92) = 3.3
    c: Equal(g89,g93) = 2.1
    c: Distance(g85,g90) = 3.36667
    c: Distance(g77,g82) = 3.36667
    c: Coincident(g96,g97)
    c: Coincident(g97,g98)
    c: Coincident(g98,g99)
    c: Coincident(g99,g96)
    c: Horizontal(g96)
    c: Horizontal(g98)
    c: Vertical(g97)
    c: Vertical(g99)
    c: Equal(g64,g96) = 3.3
    c: Equal(g65,g97) = 2.1
    c: Coincident(g100,g101)
    c: Coincident(g101,g102)
    c: Coincident(g102,g103)
    c: Coincident(g103,g100)
    c: Horizontal(g100)
    c: Horizontal(g102)
    c: Vertical(g101)
    c: Vertical(g103)
    c: Equal(g96,g100) = 3.3
    c: Equal(g97,g101) = 2.1
    c: Coincident(g104,g105)
    c: Coincident(g105,g106)
    c: Coincident(g106,g107)
    c: Coincident(g107,g104)
    c: Horizontal(g104)
    c: Horizontal(g106)
    c: Vertical(g105)
    c: Vertical(g107)
    c: Equal(g96,g104) = 3.3
    c: Equal(g97,g105) = 2.1
    c: Coincident(g108,g109)
    c: Coincident(g109,g110)
    c: Coincident(g110,g111)
    c: Coincident(g111,g108)
    c: Horizontal(g108)
    c: Horizontal(g110)
    c: Vertical(g109)
    c: Vertical(g111)
    c: Equal(g104,g108) = 3.3
    c: Equal(g105,g109) = 2.1
    c: Distance(g105,g110) = 3.36667
    c: Distance(g101,g106) = 3.36667
    c: Coincident(g112,g113)
    c: Coincident(g113,g114)
    c: Coincident(g114,g115)
    c: Coincident(g115,g112)
    c: Horizontal(g112)
    c: Horizontal(g114)
    c: Vertical(g113)
    c: Vertical(g115)
    c: Equal(g96,g112) = 3.3
    c: Equal(g97,g113) = 2.1
    c: Coincident(g116,g117)
    c: Coincident(g117,g118)
    c: Coincident(g118,g119)
    c: Coincident(g119,g116)
    c: Horizontal(g116)
    c: Horizontal(g118)
    c: Vertical(g117)
    c: Vertical(g119)
    c: Equal(g112,g116) = 3.3
    c: Equal(g113,g117) = 2.1
    c: Distance(g113,g118) = 3.36667
    c: Coincident(g120,g121)
    c: Coincident(g121,g122)
    c: Coincident(g122,g123)
    c: Coincident(g123,g120)
    c: Horizontal(g120)
    c: Horizontal(g122)
    c: Vertical(g121)
    c: Vertical(g123)
    c: Equal(g112,g120) = 3.3
    c: Equal(g113,g121) = 2.1
    c: Distance(g117,g122) = 3.36667
    c: Distance(g109,g114) = 3.36667
    c: Distance(g66,g3) = 1.68333
    c: Distance(g64,g5) = 3
    c: Distance(g68,g9) = 3
    c: Distance(g72,g13) = 3
    c: Distance(g76,g17) = 3
    c: Distance(g80,g21) = 3
    c: Distance(g84,g25) = 3
    c: Distance(g88,g29) = 3
    c: Distance(g100,g41) = 3
    c: Distance(g104,g45) = 3
    c: Distance(g108,g49) = 3
    c: Distance(g112,g53) = 3
    c: Distance(g116,g57) = 3
    c: Distance(g120,g61) = 3
    c: Distance(g92,g33) = 3
    c: Distance(g94,g89) = 3.36667
    c: Coincident(g124,g125)
    c: Coincident(g125,g126)
    c: Coincident(g126,g127)
    c: Coincident(g127,g124)
    c: Horizontal(g124)
    c: Horizontal(g126)
    c: Vertical(g125)
    c: Vertical(g127)
    c: Coincident(g128,g129)
    c: Coincident(g129,g130)
    c: Coincident(g130,g131)
    c: Coincident(g131,g128)
    c: Horizontal(g128)
    c: Horizontal(g130)
    c: Vertical(g129)
    c: Vertical(g131)
    c: Equal(g124,g128) = 3.3
    c: Equal(g125,g129) = 2.1
    c: Distance(g125,g130) = 3.36667
    c: Coincident(g132,g133)
    c: Coincident(g133,g134)
    c: Coincident(g134,g135)
    c: Coincident(g135,g132)
    c: Horizontal(g132)
    c: Horizontal(g134)
    c: Vertical(g133)
    c: Vertical(g135)
    c: Equal(g124,g132) = 3.3
    c: Equal(g125,g133) = 2.1
    c: Coincident(g136,g137)
    c: Coincident(g137,g138)
    c: Coincident(g138,g139)
    c: Coincident(g139,g136)
    c: Horizontal(g136)
    c: Horizontal(g138)
    c: Vertical(g137)
    c: Vertical(g139)
    c: Equal(g132,g136) = 3.3
    c: Equal(g133,g137) = 2.1
    c: Distance(g133,g138) = 3.36667
    c: Distance(g129,g134) = 3.36667
    c: Coincident(g140,g141)
    c: Coincident(g141,g142)
    c: Coincident(g142,g143)
    c: Coincident(g143,g140)
    c: Horizontal(g140)
    c: Horizontal(g142)
    c: Vertical(g141)
    c: Vertical(g143)
    c: Equal(g124,g140) = 3.3
    c: Equal(g125,g141) = 2.1
    c: Coincident(g144,g145)
    c: Coincident(g145,g146)
    c: Coincident(g146,g147)
    c: Coincident(g147,g144)
    c: Horizontal(g144)
    c: Horizontal(g146)
    c: Vertical(g145)
    c: Vertical(g147)
    c: Equal(g140,g144) = 3.3
    c: Equal(g141,g145) = 2.1
    c: Distance(g141,g146) = 3.36667
    c: Coincident(g148,g149)
    c: Coincident(g149,g150)
    c: Coincident(g150,g151)
    c: Coincident(g151,g148)
    c: Horizontal(g148)
    c: Horizontal(g150)
    c: Vertical(g149)
    c: Vertical(g151)
    c: Equal(g140,g148) = 3.3
    c: Equal(g141,g149) = 2.1
    c: Coincident(g152,g153)
    c: Coincident(g153,g154)
    c: Coincident(g154,g155)
    c: Coincident(g155,g152)
    c: Horizontal(g152)
    c: Horizontal(g154)
    c: Vertical(g153)
    c: Vertical(g155)
    c: Equal(g148,g152) = 3.3
    c: Equal(g149,g153) = 2.1
    c: Distance(g137,g142) = 3.36667
    c: Coincident(g156,g157)
    c: Coincident(g157,g158)
    c: Coincident(g158,g159)
    c: Coincident(g159,g156)
    c: Horizontal(g156)
    c: Horizontal(g158)
    c: Vertical(g157)
    c: Vertical(g159)
    c: Equal(g124,g156) = 3.3
    c: Equal(g125,g157) = 2.1
    c: Coincident(g160,g161)
    c: Coincident(g161,g162)
    c: Coincident(g162,g163)
    c: Coincident(g163,g160)
    c: Horizontal(g160)
    c: Horizontal(g162)
    c: Vertical(g161)
    c: Vertical(g163)
    c: Equal(g156,g160) = 3.3
    c: Equal(g157,g161) = 2.1
    c: Distance(g157,g162) = 3.36667
    c: Coincident(g164,g165)
    c: Coincident(g165,g166)
    c: Coincident(g166,g167)
    c: Coincident(g167,g164)
    c: Horizontal(g164)
    c: Horizontal(g166)
    c: Vertical(g165)
    c: Vertical(g167)
    c: Equal(g156,g164) = 3.3
    c: Equal(g157,g165) = 2.1
    c: Coincident(g168,g169)
    c: Coincident(g169,g170)
    c: Coincident(g170,g171)
    c: Coincident(g171,g168)
    c: Horizontal(g168)
    c: Horizontal(g170)
    c: Vertical(g169)
    c: Vertical(g171)
    c: Equal(g164,g168) = 3.3
    c: Equal(g165,g169) = 2.1
    c: Distance(g165,g170) = 3.36667
    c: Coincident(g172,g173)
    c: Coincident(g173,g174)
    c: Coincident(g174,g175)
    c: Coincident(g175,g172)
    c: Horizontal(g172)
    c: Horizontal(g174)
    c: Vertical(g173)
    c: Vertical(g175)
    c: Equal(g156,g172) = 3.3
    c: Equal(g157,g173) = 2.1
    c: Coincident(g176,g177)
    c: Coincident(g177,g178)
    c: Coincident(g178,g179)
    c: Coincident(g179,g176)
    c: Horizontal(g176)
    c: Horizontal(g178)
    c: Vertical(g177)
    c: Vertical(g179)
    c: Equal(g172,g176) = 3.3
    c: Equal(g173,g177) = 2.1
    c: Distance(g173,g178) = 3.36667
    c: Coincident(g180,g181)
    c: Coincident(g181,g182)
    c: Coincident(g182,g183)
    c: Coincident(g183,g180)
    c: Horizontal(g180)
    c: Horizontal(g182)
    c: Vertical(g181)
    c: Vertical(g183)
    c: Equal(g172,g180) = 3.3
    c: Equal(g173,g181) = 2.1
    c: Distance(g177,g182) = 3.36667
    c: Distance(g169,g174) = 3.36667
    c: Distance(g154,g149) = 3.36667
    c: Distance(g126,g3) = 1.68333
    c: DistanceX(g126,g126) = 3.3
    c: DistanceY(g125,g125) = 2.1
    c: Distance(g124,g65) = 3
    c: DistanceY(g69,g128) = 3
    c: DistanceY(g73,g132) = 3
    c: DistanceY(g77,g136) = 3
    c: Distance(g152,g93) = 3
    c: Distance(g140,g81) = 3
    c: Distance(g144,g85) = 3
    c: Distance(g156,g97) = 3
    c: Distance(g180,g121) = 3
    c: Distance(g176,g117) = 3
    c: Distance(g172,g113) = 3
    c: Distance(g168,g109) = 3
    c: Distance(g164,g105) = 3
    c: Distance(g158,g153) = 3.36667
    c: Distance(g166,g161) = 3.36667
    c: Distance(g160,g101) = 3
    c: Coincident(g184,g185)
    c: Coincident(g185,g186)
    c: Coincident(g186,g187)
    c: Coincident(g187,g184)
    c: Horizontal(g184)
    c: Horizontal(g186)
    c: Vertical(g185)
    c: Vertical(g187)
    c: Coincident(g188,g189)
    c: Coincident(g189,g190)
    c: Coincident(g190,g191)
    c: Coincident(g191,g188)
    c: Horizontal(g188)
    c: Horizontal(g190)
    c: Vertical(g189)
    c: Vertical(g191)
    c: Coincident(g192,g193)
    c: Coincident(g193,g194)
    c: Coincident(g194,g195)
    c: Coincident(g195,g192)
    c: Horizontal(g192)
    c: Horizontal(g194)
    c: Vertical(g193)
    c: Vertical(g195)
    c: Equal(g188,g192) = 3.3
    c: Equal(g189,g193) = 2.1
    c: Distance(g189,g194) = 5.03333
    c: Coincident(g196,g197)
    c: Coincident(g197,g198)
    c: Coincident(g198,g199)
    c: Coincident(g199,g196)
    c: Horizontal(g196)
    c: Horizontal(g198)
    c: Vertical(g197)
    c: Vertical(g199)
    c: Equal(g188,g196) = 3.3
    c: Equal(g189,g197) = 2.1
    c: Coincident(g200,g201)
    c: Coincident(g201,g202)
    c: Coincident(g202,g203)
    c: Coincident(g203,g200)
    c: Horizontal(g200)
    c: Horizontal(g202)
    c: Vertical(g201)
    c: Vertical(g203)
    c: Equal(g196,g200) = 3.3
    c: Equal(g197,g201) = 2.1
    c: Distance(g185,g190) = 5.03333
    c: Coincident(g204,g205)
    c: Coincident(g205,g206)
    c: Coincident(g206,g207)
    c: Coincident(g207,g204)
    c: Horizontal(g204)
    c: Horizontal(g206)
    c: Vertical(g205)
    c: Vertical(g207)
    c: Coincident(g208,g209)
    c: Coincident(g209,g210)
    c: Coincident(g210,g211)
    c: Coincident(g211,g208)
    c: Horizontal(g208)
    c: Horizontal(g210)
    c: Vertical(g209)
    c: Vertical(g211)
    c: Equal(g204,g208) = 3.3
    c: Equal(g205,g209) = 2.1
    c: Distance(g205,g210) = 5.03333
    c: Coincident(g212,g213)
    c: Coincident(g213,g214)
    c: Coincident(g214,g215)
    c: Coincident(g215,g212)
    c: Horizontal(g212)
    c: Horizontal(g214)
    c: Vertical(g213)
    c: Vertical(g215)
    c: Equal(g204,g212) = 3.3
    c: Equal(g205,g213) = 2.1
    c: Coincident(g216,g217)
    c: Coincident(g217,g218)
    c: Coincident(g218,g219)
    c: Coincident(g219,g216)
    c: Horizontal(g216)
    c: Horizontal(g218)
    c: Vertical(g217)
    c: Vertical(g219)
    c: Equal(g212,g216) = 3.3
    c: Equal(g213,g217) = 2.1
    c: Distance(g213,g218) = 5.03333
    c: Coincident(g220,g221)
    c: Coincident(g221,g222)
    c: Coincident(g222,g223)
    c: Coincident(g223,g220)
    c: Horizontal(g220)
    c: Horizontal(g222)
    c: Vertical(g221)
    c: Vertical(g223)
    c: Equal(g204,g220) = 3.3
    c: Equal(g205,g221) = 2.1
    c: Coincident(g224,g225)
    c: Coincident(g225,g226)
    c: Coincident(g226,g227)
    c: Coincident(g227,g224)
    c: Horizontal(g224)
    c: Horizontal(g226)
    c: Vertical(g225)
    c: Vertical(g227)
    c: Equal(g220,g224) = 3.3
    c: Equal(g221,g225) = 2.1
    c: Distance(g221,g226) = 5.03333
    c: Coincident(g228,g229)
    c: Coincident(g229,g230)
    c: Coincident(g230,g231)
    c: Coincident(g231,g228)
    c: Horizontal(g228)
    c: Horizontal(g230)
    c: Vertical(g229)
    c: Vertical(g231)
    c: Equal(g220,g228) = 3.3
    c: Equal(g221,g229) = 2.1
    c: Distance(g225,g230) = 5.03333
    c: Distance(g217,g222) = 5.03333
    c: Distance(g202,g197) = 5.03333
    c: Distance(g206,g201) = 5.03333
    c: Distance(g214,g209) = 5.03333
    c: DistanceY(g187,g187) = 2.1
    c: DistanceX(g186,g186) = 3.3
    c: Distance(g186,g3) = 2.51667
    c: DistanceY(g229,g229) = 2.1
    c: DistanceX(g228,g228) = 3.3
    c: Distance(g229,g1) = 2.51667
    c: DistanceX(g190,g190) = 3.3
    c: DistanceY(g189,g189) = 2.1
    c: DistanceY(g89,g148) = 3
    c: DistanceY(g42,g96) = 3
    c: DistanceX(g96,g100) = 3.36667
    c: DistanceX(g93,g98) = 3.36667
    c: DistanceX(g145,g150) = 3.36667
    c: Coincident(g232,g233)
    c: Coincident(g233,g234)
    c: Coincident(g234,g235)
    c: Coincident(g235,g232)
    c: Horizontal(g232)
    c: Horizontal(g234)
    c: Vertical(g233)
    c: Vertical(g235)
    c: Equal(g4,g232) = 3.3
    c: Equal(g5,g233) = 2.1
    c: Coincident(g236,g237)
    c: Coincident(g237,g238)
    c: Coincident(g238,g239)
    c: Coincident(g239,g236)
    c: Horizontal(g236)
    c: Horizontal(g238)
    c: Vertical(g237)
    c: Vertical(g239)
    c: Equal(g232,g236) = 3.3
    c: Equal(g233,g237) = 2.1
    c: Distance(g233,g238) = 3.36667
    c: Coincident(g240,g241)
    c: Coincident(g241,g242)
    c: Coincident(g242,g243)
    c: Coincident(g243,g240)
    c: Horizontal(g240)
    c: Horizontal(g242)
    c: Vertical(g241)
    c: Vertical(g243)
    c: Equal(g232,g240) = 3.3
    c: Equal(g233,g241) = 2.1
    c: Coincident(g244,g245)
    c: Coincident(g245,g246)
    c: Coincident(g246,g247)
    c: Coincident(g247,g244)
    c: Horizontal(g244)
    c: Horizontal(g246)
    c: Vertical(g245)
    c: Vertical(g247)
    c: Equal(g240,g244) = 3.3
    c: Equal(g241,g245) = 2.1
    c: Distance(g241,g246) = 3.36667
    c: Distance(g237,g242) = 3.36667
    c: Coincident(g248,g249)
    c: Coincident(g249,g250)
    c: Coincident(g250,g251)
    c: Coincident(g251,g248)
    c: Horizontal(g248)
    c: Horizontal(g250)
    c: Vertical(g249)
    c: Vertical(g251)
    c: Equal(g232,g248) = 3.3
    c: Equal(g233,g249) = 2.1
    c: Coincident(g252,g253)
    c: Coincident(g253,g254)
    c: Coincident(g254,g255)
    c: Coincident(g255,g252)
    c: Horizontal(g252)
    c: Horizontal(g254)
    c: Vertical(g253)
    c: Vertical(g255)
    c: Equal(g248,g252) = 3.3
    c: Equal(g249,g253) = 2.1
    c: Distance(g249,g254) = 3.36667
    c: Coincident(g256,g257)
    c: Coincident(g257,g258)
    c: Coincident(g258,g259)
    c: Coincident(g259,g256)
    c: Horizontal(g256)
    c: Horizontal(g258)
    c: Vertical(g257)
    c: Vertical(g259)
    c: Equal(g248,g256) = 3.3
    c: Equal(g249,g257) = 2.1
    c: Coincident(g260,g261)
    c: Coincident(g261,g262)
    c: Coincident(g262,g263)
    c: Coincident(g263,g260)
    c: Horizontal(g260)
    c: Horizontal(g262)
    c: Vertical(g261)
    c: Vertical(g263)
    c: Equal(g256,g260) = 3.3
    c: Equal(g257,g261) = 2.1
    c: Distance(g257,g262) = 3.36667
    c: Distance(g253,g258) = 3.36667
    c: Distance(g245,g250) = 3.36667
    c: Coincident(g264,g265)
    c: Coincident(g265,g266)
    c: Coincident(g266,g267)
    c: Coincident(g267,g264)
    c: Horizontal(g264)
    c: Horizontal(g266)
    c: Vertical(g265)
    c: Vertical(g267)
    c: Equal(g232,g264) = 3.3
    c: Equal(g233,g265) = 2.1
    c: Coincident(g268,g269)
    c: Coincident(g269,g270)
    c: Coincident(g270,g271)
    c: Coincident(g271,g268)
    c: Horizontal(g268)
    c: Horizontal(g270)
    c: Vertical(g269)
    c: Vertical(g271)
    c: Equal(g264,g268) = 3.3
    c: Equal(g265,g269) = 2.1
    c: Distance(g265,g270) = 3.36667
    c: Coincident(g272,g273)
    c: Coincident(g273,g274)
    c: Coincident(g274,g275)
    c: Coincident(g275,g272)
    c: Horizontal(g272)
    c: Horizontal(g274)
    c: Vertical(g273)
    c: Vertical(g275)
    c: Equal(g264,g272) = 3.3
    c: Equal(g265,g273) = 2.1
    c: Coincident(g276,g277)
    c: Coincident(g277,g278)
    c: Coincident(g278,g279)
    c: Coincident(g279,g276)
    c: Horizontal(g276)
    c: Horizontal(g278)
    c: Vertical(g277)
    c: Vertical(g279)
    c: Equal(g272,g276) = 3.3
    c: Equal(g273,g277) = 2.1
    c: Distance(g273,g278) = 3.36667
    c: Distance(g269,g274) = 3.36667
    c: Coincident(g280,g281)
    c: Coincident(g281,g282)
    c: Coincident(g282,g283)
    c: Coincident(g283,g280)
    c: Horizontal(g280)
    c: Horizontal(g282)
    c: Vertical(g281)
    c: Vertical(g283)
    c: Equal(g264,g280) = 3.3
    c: Equal(g265,g281) = 2.1
    c: Coincident(g284,g285)
    c: Coincident(g285,g286)
    c: Coincident(g286,g287)
    c: Coincident(g287,g284)
    c: Horizontal(g284)
    c: Horizontal(g286)
    c: Vertical(g285)
    c: Vertical(g287)
    c: Equal(g280,g284) = 3.3
    c: Equal(g281,g285) = 2.1
    c: Distance(g281,g286) = 3.36667
    c: Coincident(g288,g289)
    c: Coincident(g289,g290)
    c: Coincident(g290,g291)
    c: Coincident(g291,g288)
    c: Horizontal(g288)
    c: Horizontal(g290)
    c: Vertical(g289)
    c: Vertical(g291)
    c: Equal(g280,g288) = 3.3
    c: Equal(g281,g289) = 2.1
    c: Distance(g285,g290) = 3.36667
    c: Distance(g277,g282) = 3.36667
    c: Distance(g261,g266) = 3.36667
    c: DistanceX(g0,g234) = 1.68333
    c: DistanceY(g125,g232) = 3
    c: DistanceY(g129,g236) = 3
    c: DistanceY(g133,g240) = 3
    c: DistanceY(g137,g244) = 3
    c: DistanceY(g141,g248) = 3
    c: DistanceY(g145,g252) = 3
    c: DistanceY(g149,g256) = 3
    c: DistanceY(g153,g260) = 3
    c: DistanceY(g157,g264) = 3
    c: DistanceY(g161,g268) = 3
    c: DistanceY(g165,g272) = 3
    c: DistanceY(g169,g276) = 3
    c: DistanceY(g173,g280) = 3
    c: DistanceY(g177,g284) = 3
    c: DistanceY(g181,g288) = 3
    c: DistanceY(g0,g184) = 25.5
    c: DistanceY(g188,g184) = 0
    c: DistanceY(g192,g188) = 0
    c: DistanceY(g196,g192) = 0
    c: DistanceY(g0,g228) = 25.5
    c: DistanceY(g224,g228) = 0
    c: DistanceY(g220,g224) = 0
    c: DistanceY(g216,g220) = 0
    c: DistanceY(g212,g216) = 0
    c: DistanceY(g208,g212) = 0
    c: DistanceY(g204,g208) = 0
    c: DistanceY(g200,g196) = 0
FEATURE [PartDesign::Body] Body
  Group = -> [Sketch]
  Origin = -> Origin
